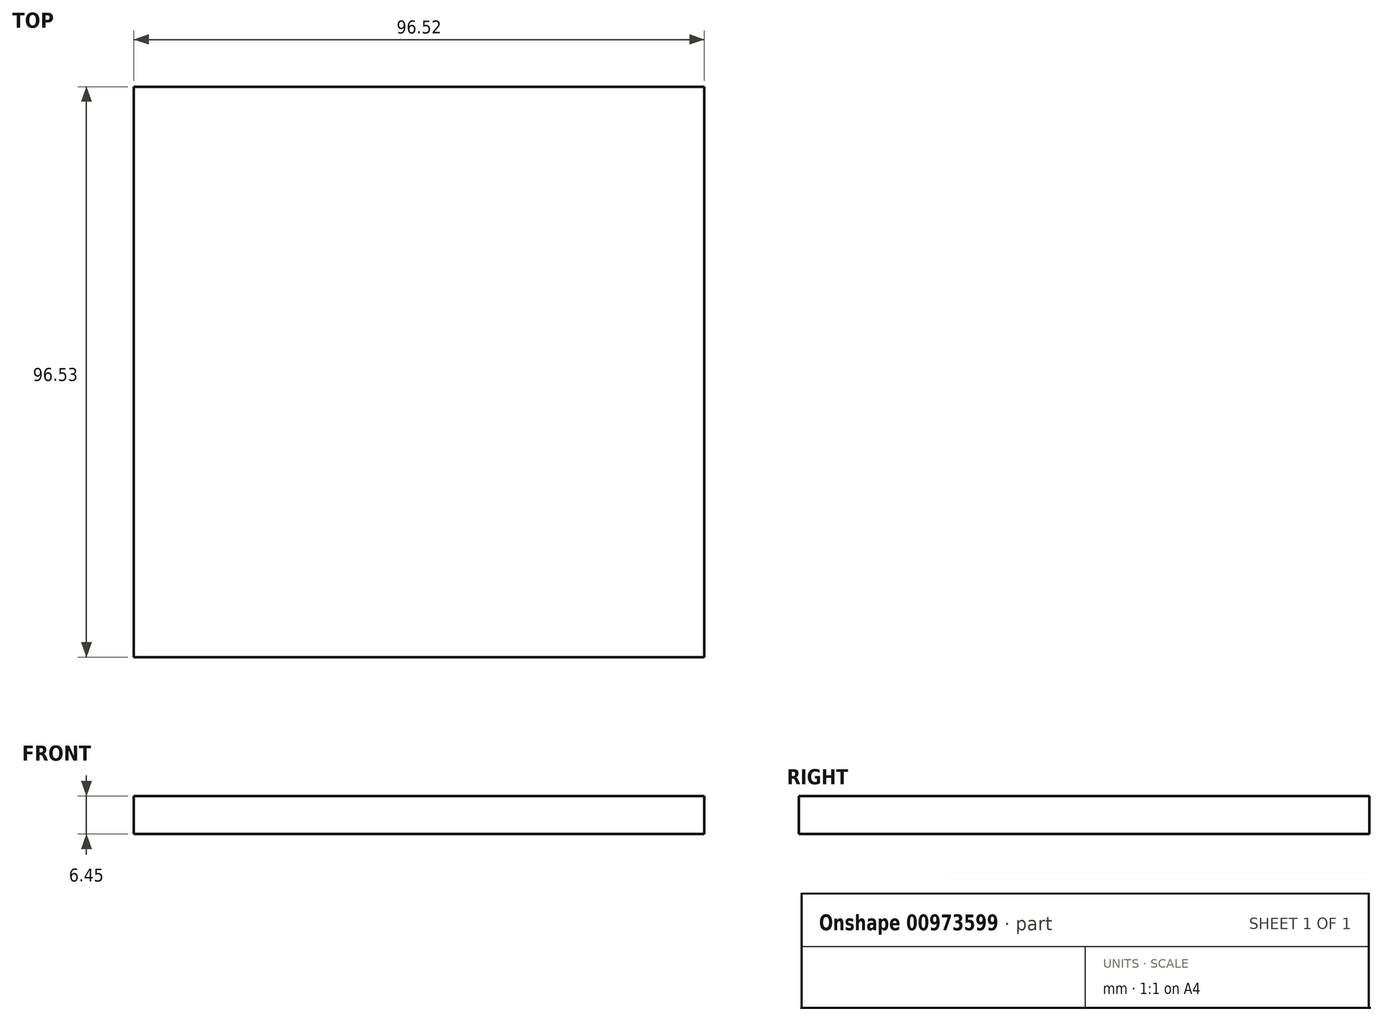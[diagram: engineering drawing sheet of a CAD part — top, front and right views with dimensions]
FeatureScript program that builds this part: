
annotation { "Feature Type Name" : "Feature", "Feature Type Description" : "" }
export const myFeature = defineFeature(function(context is Context, id is Id, definition is map)
    precondition{}
    {
        {
            var Q0;
            Q0=qCreatedBy(makeId("Top.planeOp"),FACE);
            var sketch = newSketch(context, id + "F0", { "sketchPlane" : qUnion([Q0])});
            skLineSegment(sketch, "E0", {"start": v(-39.89, 38.96) * mm, "end": v(56.63, 38.96) * mm});
            skLineSegment(sketch, "E1", {"start": v(56.63, 38.96) * mm, "end": v(56.63, -57.57) * mm});
            skLineSegment(sketch, "E2", {"start": v(56.63, -57.57) * mm, "end": v(-39.89, -57.57) * mm});
            skLineSegment(sketch, "E3", {"start": v(-39.89, -57.57) * mm, "end": v(-39.89, 38.96) * mm});
            skSolve(sketch);
        }
        {
            var Q0;
            Q0=makeQuery(id+"F0.imprint","IMPRINT",FACE,{"disambiguationData":[TD([[makeQuery(id+"F0.imprint","IMPRINT",EDGE,{"derivedFrom":sQuery(id+"F0.wireOp",EDGE,"E0")}),-1.0]])]});
            extrude(context, id + "F1", {"entities" : qUnion([Q0]), "depth" : 6.45 * mm, "offsetDistance" : 25.4 * mm});
        }
    });
